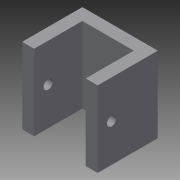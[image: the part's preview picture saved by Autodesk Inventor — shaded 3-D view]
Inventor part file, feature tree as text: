
AUTODESK INVENTOR PART (.ipt)
format: ipt  version: 2013 (Build 170138000, 138)  size: 93,184 bytes
history: native  units: in
note: dims shown in document units (in); Inventor stores cm internally (conversion verified against a paired STEP export)
features: extrude x4, sketch x4
ambient origin geometry x8: Origin, YZ Plane, XZ Plane, XY Plane, X Axis, Y Axis, Z Axis, Center Point
bodies: Solid1 (feature_tree)
feature tree (8):
  extrude  "Extrusion1"  Depth=1.5748in
  extrude  "Extrusion2"  Depth=0.25in
  extrude  "Extrusion3"  Depth=0.25in
  extrude  "Extrusion4"  Depth=0.19in
  sketch  "Sketch1"  dims[d0=1.68in d1=1.5748in]
  sketch  "Sketch2"  dims[d2=0.25in d3=0.0in d4=0.25in]
  sketch  "Sketch3"  dims[d5=1.0in d6=0.0in d7=0.25in]
  sketch  "Sketch4"  dims[d8=1.0in d9=0.0in d10=0.19in d11=3.0in d12=0.0in]
